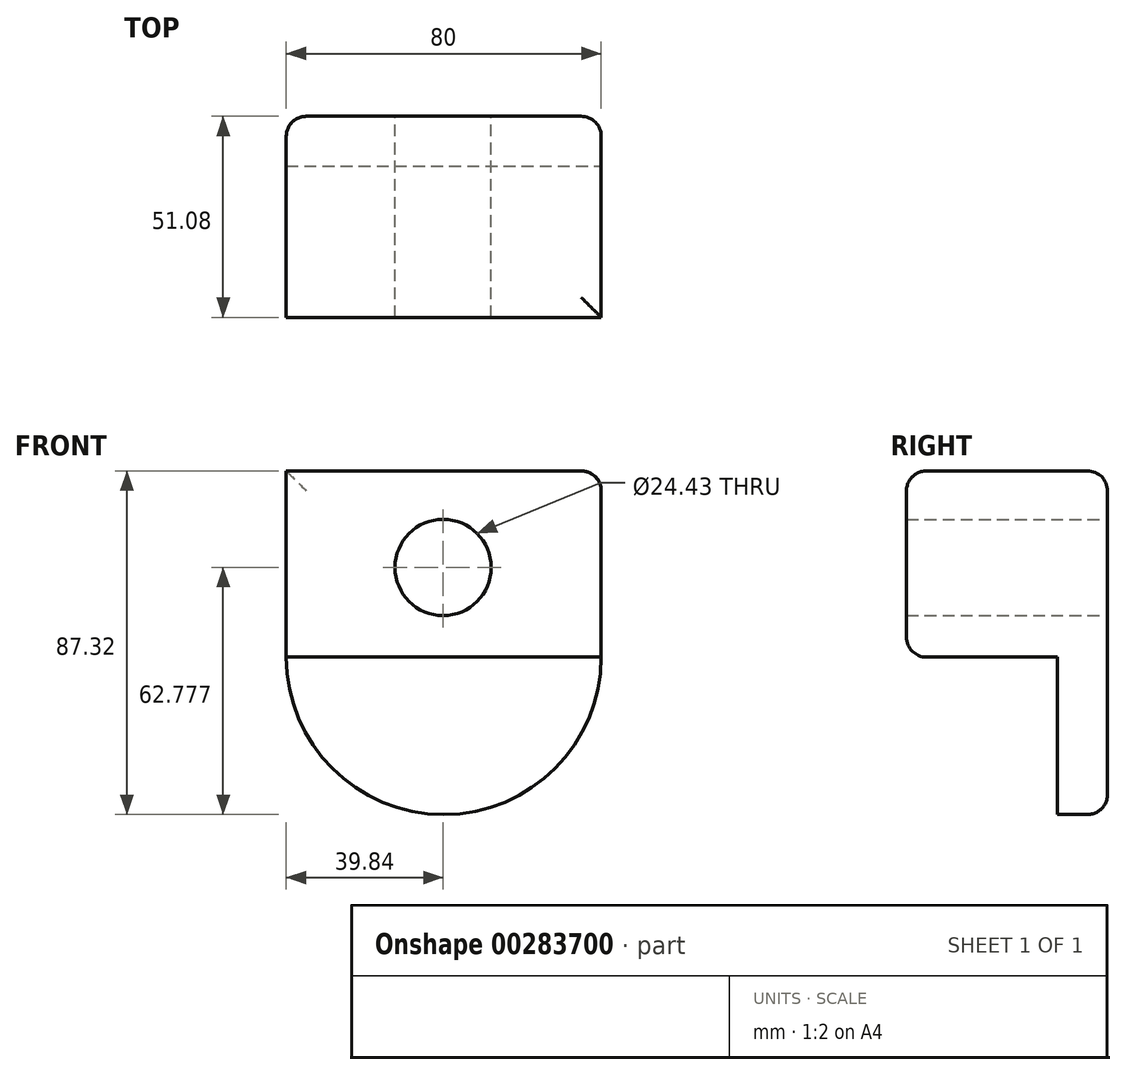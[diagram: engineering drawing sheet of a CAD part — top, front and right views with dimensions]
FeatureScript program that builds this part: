
annotation { "Feature Type Name" : "Feature", "Feature Type Description" : "" }
export const myFeature = defineFeature(function(context is Context, id is Id, definition is map)
    precondition{}
    {
        {
            var Q0;
            Q0=qCreatedBy(makeId("Front.planeOp"),FACE);
            var sketch = newSketch(context, id + "F0", { "sketchPlane" : qUnion([Q0])});
            skLineSegment(sketch, "E0", {"start": v(-51.77, 48.1) * mm, "end": v(28.23, 48.1) * mm});
            skLineSegment(sketch, "E1", {"start": v(-51.77, 48.1) * mm, "end": v(-51.77, 0.78) * mm});
            skLineSegment(sketch, "E2", {"start": v(28.23, 48.1) * mm, "end": v(28.23, 0.78) * mm});
            skArc(sketch, "E3", {"start": v(-51.77, 0.78) * mm, "mid": v(-11.77, -39.22) * mm, "end": v(28.23, 0.78) * mm});
            skCircle(sketch, "E4", {"center": v(-11.93, 23.56) * mm, "radius": 12.22 * mm});
            skLineSegment(sketch, "E5", {"start": v(-51.77, 0.78) * mm, "end": v(28.23, 0.78) * mm});
            skSolve(sketch);
        }
        {
            var Q0;
            Q0=makeQuery(id+"F0.imprint","IMPRINT",FACE,{"disambiguationData":[TD([[makeQuery(id+"F0.imprint","IMPRINT",EDGE,{"derivedFrom":sQuery(id+"F0.wireOp",EDGE,"E0")}),-1.0]])]});
            extrude(context, id + "F1", {"entities" : qUnion([Q0]), "depth" : 51.08 * mm});
        }
        {
            var Q0;
            Q0=makeQuery(id+"F0.imprint","IMPRINT",FACE,{"disambiguationData":[TD([[makeQuery(id+"F0.imprint","IMPRINT",EDGE,{"derivedFrom":sQuery(id+"F0.wireOp",EDGE,"E3")}),1.0]])]});
            extrude(context, id + "F2", {"entities" : qUnion([Q0]), "operationType" : NewBodyOperationType.ADD, "depth" : 12.7 * mm});
        }
        {
            var Q0;
            Q0=makeQuery(id+"F1.opExtrude","SWEPT_EDGE",EDGE,{"disambiguationData":[OSD([sQuery(id+"F0.wireOp",EDGE,"E0"),sQuery(id+"F0.wireOp",EDGE,"E2")])]});
            var Q1;
            Q1=makeQuery(id+"F1.opExtrude","CAP_EDGE",EDGE,{"disambiguationData":[OSD([sQuery(id+"F0.wireOp",EDGE,"E5")])],"isStart":false});
            var Q2;
            Q2=makeQuery(id+"F1.opExtrude","CAP_EDGE",EDGE,{"disambiguationData":[OSD([sQuery(id+"F0.wireOp",EDGE,"E0")])],"isStart":false});
            fillet(context, id + "F3", {"entities" : qUnion([Q0, Q1, Q2]), "radius" : 5.08 * mm, "tangentPropagation" : true, "allowEdgeOverflow" : false});
        }
        {
            var Q0;
            Q0=makeQuery(id+"F1.opExtrude","CAP_EDGE",EDGE,{"disambiguationData":[OSD([sQuery(id+"F0.wireOp",EDGE,"E0")])],"isStart":true});
            fillet(context, id + "F4", {"entities" : qUnion([Q0]), "radius" : 5.08 * mm, "tangentPropagation" : true, "allowEdgeOverflow" : false});
        }
    });
